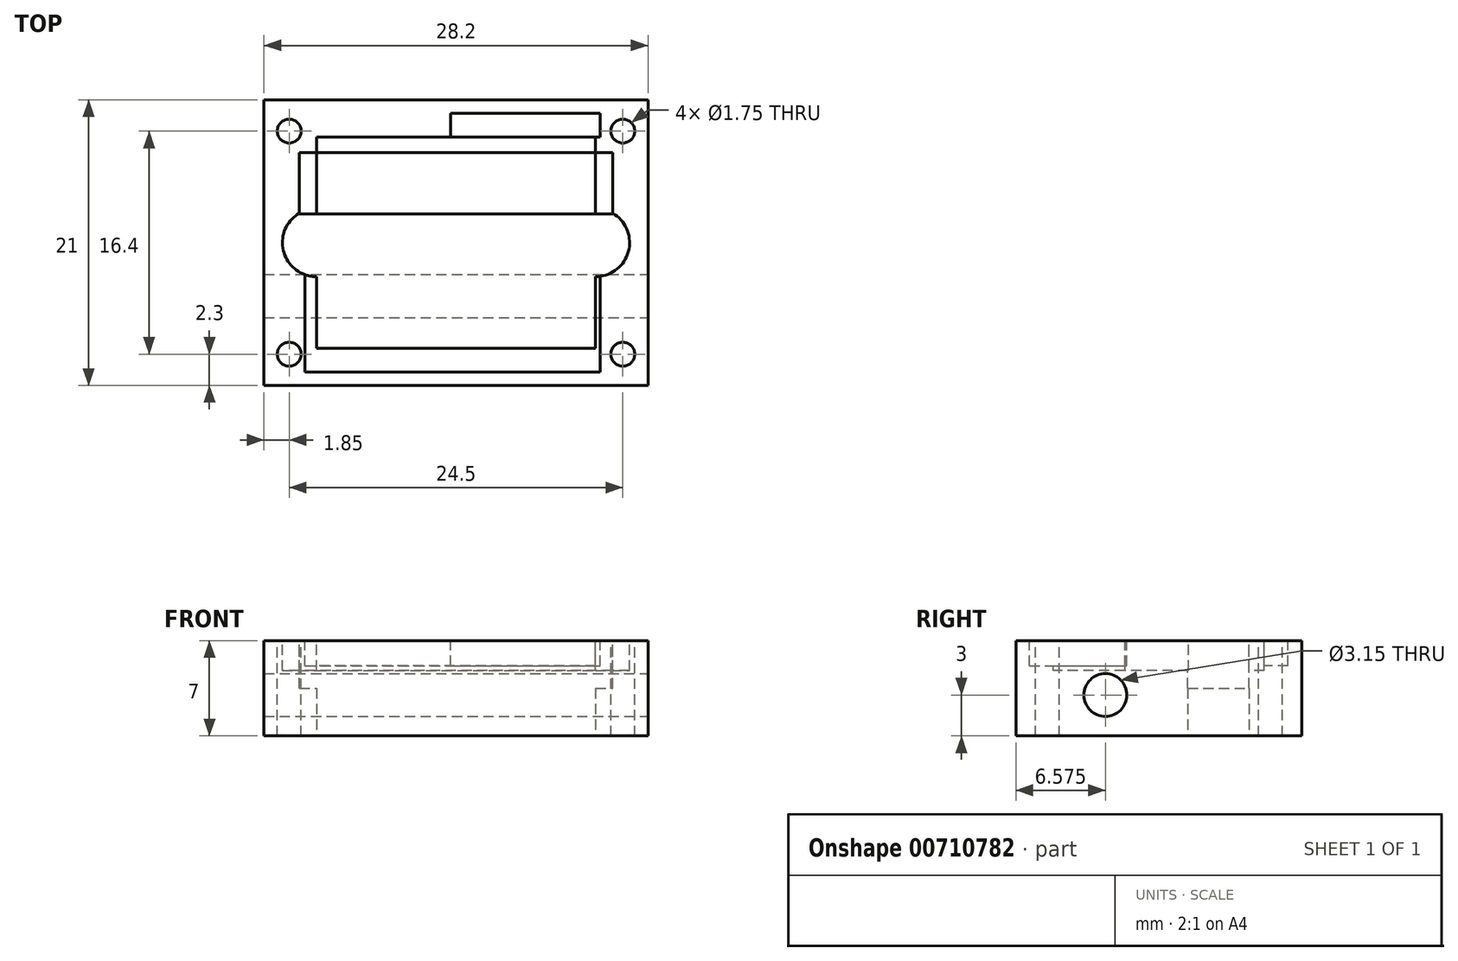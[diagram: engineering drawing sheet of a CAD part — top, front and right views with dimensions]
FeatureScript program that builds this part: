
annotation { "Feature Type Name" : "Feature", "Feature Type Description" : "" }
export const myFeature = defineFeature(function(context is Context, id is Id, definition is map)
    precondition{}
    {
        {
            var Q0;
            Q0=qCreatedBy(makeId("Top.planeOp"),FACE);
            var sketch = newSketch(context, id + "F0", { "sketchPlane" : qUnion([Q0])});
            skLineSegment(sketch, "E0.bottom", {"start": v(-14.1, 10.5) * mm, "end": v(14.1, 10.5) * mm});
            skLineSegment(sketch, "E0.top", {"start": v(-14.1, -10.5) * mm, "end": v(14.1, -10.5) * mm});
            skLineSegment(sketch, "E0.left", {"start": v(-14.1, 10.5) * mm, "end": v(-14.1, -10.5) * mm});
            skLineSegment(sketch, "E0.right", {"start": v(14.1, 10.5) * mm, "end": v(14.1, -10.5) * mm});
            skPoint(sketch, "E0.middle", {"position": v(0, 0) * mm});
            skSolve(sketch);
        }
        {
            var Q0;
            Q0 = qSketchRegion(id + "F0", true);
            extrude(context, id + "F1", {"entities" : qUnion([Q0]), "endBound" : BoundingType.SYMMETRIC, "depth" : 8 * mm, "offsetDistance" : 25 * mm});
        }
        {
            var Q0;
            Q0=makeQuery(id+"F1.opExtrude","CAP_FACE",FACE,{"disambiguationData":[OSD([sQuery(id+"F0.wireOp",EDGE,"E0.bottom"),sQuery(id+"F0.wireOp",EDGE,"E0.top"),sQuery(id+"F0.wireOp",EDGE,"E0.left"),sQuery(id+"F0.wireOp",EDGE,"E0.right")])],"isStart":false});
            var sketch = newSketch(context, id + "F2", { "sketchPlane" : qUnion([Q0])});
            skLineSegment(sketch, "E1.bottom", {"start": v(-10.25, 7.75) * mm, "end": v(10.25, 7.75) * mm});
            skLineSegment(sketch, "E1.top", {"start": v(-10.25, -7.75) * mm, "end": v(10.25, -7.75) * mm});
            skLineSegment(sketch, "E1.left", {"start": v(-10.25, 7.75) * mm, "end": v(-10.25, -7.75) * mm});
            skLineSegment(sketch, "E1.right", {"start": v(10.25, 7.75) * mm, "end": v(10.25, -7.75) * mm});
            skPoint(sketch, "E1.middle", {"position": v(0, 0) * mm});
            skCircle(sketch, "E2", {"center": v(-10.25, 0) * mm, "radius": 2.5 * mm});
            skCircle(sketch, "E3", {"center": v(10.25, 0) * mm, "radius": 2.5 * mm});
            skSolve(sketch);
        }
        {
            var Q0;
            Q0 = qSketchRegion(id + "F2", true);
            var Q1;
            Q1 = qSketchRegion(id + "F5", true);
            extrude(context, id + "F3", {"entities" : qUnion([Q0, Q1]), "operationType" : NewBodyOperationType.REMOVE, "oppositeDirection" : true, "depth" : 2.2 * mm, "offsetDistance" : 25 * mm});
        }
        {
            var Q0;
            Q0=makeQuery(id+"F1.opExtrude","CAP_FACE",FACE,{"disambiguationData":[OSD([sQuery(id+"F0.wireOp",EDGE,"E0.bottom"),sQuery(id+"F0.wireOp",EDGE,"E0.top"),sQuery(id+"F0.wireOp",EDGE,"E0.left"),sQuery(id+"F0.wireOp",EDGE,"E0.right")])],"isStart":false});
            var sketch = newSketch(context, id + "F4", { "sketchPlane" : qUnion([Q0])});
            skLineSegment(sketch, "E4.bottom", {"start": v(-12.25, 8.2) * mm, "end": v(12.25, 8.2) * mm});
            skLineSegment(sketch, "E4.top", {"start": v(-12.25, -8.2) * mm, "end": v(12.25, -8.2) * mm});
            skLineSegment(sketch, "E4.left", {"start": v(-12.25, 8.2) * mm, "end": v(-12.25, -8.2) * mm});
            skLineSegment(sketch, "E4.right", {"start": v(12.25, 8.2) * mm, "end": v(12.25, -8.2) * mm});
            skPoint(sketch, "E4.middle", {"position": v(0, 0) * mm});
            skSolve(sketch);
        }
        {
            var Q0;
            Q0=makeQuery(id+"F4.imprint","IMPRINT",FACE,{"disambiguationData":[TD([[makeQuery(id+"F4.imprint","IMPRINT",EDGE,{"derivedFrom":sQuery(id+"F4.wireOp",EDGE,"E4.bottom")}),1.0]])]});
            var sketch = newSketch(context, id + "F5", { "sketchPlane" : qUnion([Q0])});
            skCircle(sketch, "E5", {"center": v(-12.25, 8.2) * mm, "radius": 0.88 * mm});
            skCircle(sketch, "E6", {"center": v(12.25, 8.2) * mm, "radius": 0.88 * mm});
            skCircle(sketch, "E7", {"center": v(12.25, -8.2) * mm, "radius": 0.88 * mm});
            skCircle(sketch, "E8", {"center": v(-12.25, -8.2) * mm, "radius": 0.88 * mm});
            skSolve(sketch);
        }
        {
            var Q0;
            Q0 = qSketchRegion(id + "F5", true);
            extrude(context, id + "F6", {"entities" : qUnion([Q0]), "operationType" : NewBodyOperationType.REMOVE, "oppositeDirection" : true, "depth" : 25 * mm, "offsetDistance" : 25 * mm});
        }
        {
            var Q0;
            Q0=qCreatedBy(makeId("Top.planeOp"),FACE);
            var sketch = newSketch(context, id + "F7", { "sketchPlane" : qUnion([Q0])});
            skLineSegment(sketch, "E9.bottom", {"start": v(-10.25, 6.62) * mm, "end": v(10.25, 6.62) * mm});
            skLineSegment(sketch, "E9.top", {"start": v(-10.25, 2.12) * mm, "end": v(10.25, 2.12) * mm});
            skLineSegment(sketch, "E9.left", {"start": v(-10.25, 6.62) * mm, "end": v(-10.25, 2.12) * mm});
            skLineSegment(sketch, "E9.right", {"start": v(10.25, 6.62) * mm, "end": v(10.25, 2.12) * mm});
            skSolve(sketch);
        }
        {
            var Q0;
            Q0 = qSketchRegion(id + "F7", true);
            extrude(context, id + "F8", {"entities" : qUnion([Q0]), "operationType" : NewBodyOperationType.REMOVE, "endBound" : BoundingType.SYMMETRIC, "depth" : 55 * mm, "offsetDistance" : 25 * mm});
        }
        {
            var Q0;
            Q0=makeQuery(id+"F1.opExtrude","SWEPT_FACE",FACE,{"disambiguationData":[OSD([sQuery(id+"F0.wireOp",EDGE,"E0.right")])]});
            var sketch = newSketch(context, id + "F9", { "sketchPlane" : qUnion([Q0])});
            skCircle(sketch, "E10", {"center": v(-3.93, 0) * mm, "radius": 1.58 * mm});
            skSolve(sketch);
        }
        {
            var Q0;
            Q0 = qSketchRegion(id + "F9", true);
            extrude(context, id + "F10", {"entities" : qUnion([Q0]), "operationType" : NewBodyOperationType.REMOVE, "oppositeDirection" : true, "depth" : 29 * mm, "offsetDistance" : 25 * mm});
        }
        {
            var Q0;
            Q0=makeQuery(id+"F1.opExtrude","SWEPT_FACE",FACE,{"disambiguationData":[OSD([sQuery(id+"F0.wireOp",EDGE,"E0.right")])]});
            var sketch = newSketch(context, id + "F11", { "sketchPlane" : qUnion([Q0])});
            skLineSegment(sketch, "E11.bottom", {"start": v(-10.5, -4) * mm, "end": v(10.5, -4) * mm});
            skLineSegment(sketch, "E11.top", {"start": v(-10.5, -3) * mm, "end": v(10.5, -3) * mm});
            skLineSegment(sketch, "E11.left", {"start": v(-10.5, -4) * mm, "end": v(-10.5, -3) * mm});
            skLineSegment(sketch, "E11.right", {"start": v(10.5, -4) * mm, "end": v(10.5, -3) * mm});
            skSolve(sketch);
        }
        {
            var Q0;
            Q0 = qSketchRegion(id + "F11", true);
            extrude(context, id + "F12", {"entities" : qUnion([Q0]), "operationType" : NewBodyOperationType.REMOVE, "oppositeDirection" : true, "depth" : 28.2 * mm, "offsetDistance" : 25 * mm});
        }
        {
            var Q0;
            {var subQ4=sQuery(id+"F4.wireOp",EDGE,"E4.bottom");Q0=makeQuery(id+"F4.imprint","IMPRINT",FACE,{"disambiguationData":[TD([[makeQuery(id+"F4.imprint","IMPRINT",EDGE,{"derivedFrom":subQ4}),1.0]])]});}
            var sketch = newSketch(context, id + "F13", { "sketchPlane" : qUnion([Q0])});
            skLineSegment(sketch, "E12.bottom", {"start": v(-11.5, 6.62) * mm, "end": v(11.5, 6.62) * mm});
            skLineSegment(sketch, "E12.top", {"start": v(-11.5, 2.12) * mm, "end": v(11.5, 2.12) * mm});
            skLineSegment(sketch, "E12.left", {"start": v(-11.5, 6.62) * mm, "end": v(-11.5, 2.12) * mm});
            skLineSegment(sketch, "E12.right", {"start": v(11.5, 6.62) * mm, "end": v(11.5, 2.12) * mm});
            skSolve(sketch);
        }
        {
            var Q0;
            Q0 = qSketchRegion(id + "F13", true);
            extrude(context, id + "F14", {"entities" : qUnion([Q0]), "operationType" : NewBodyOperationType.REMOVE, "oppositeDirection" : true, "depth" : 3.5 * mm, "offsetDistance" : 25 * mm});
        }
        {
            var Q0;
            Q0 = qSketchRegion(id + "F13", true);
            extrude(context, id + "F15", {"entities" : qUnion([Q0]), "operationType" : NewBodyOperationType.REMOVE, "oppositeDirection" : true, "depth" : 3 * mm, "offsetDistance" : 25 * mm});
        }
        {
            var Q0;
            {var subQ4=sQuery(id+"F4.wireOp",EDGE,"E4.bottom");Q0=makeQuery(id+"F4.imprint","IMPRINT",FACE,{"disambiguationData":[TD([[makeQuery(id+"F4.imprint","IMPRINT",EDGE,{"derivedFrom":subQ4}),1.0]])]});}
            var sketch = newSketch(context, id + "F16", { "sketchPlane" : qUnion([Q0])});
            skLineSegment(sketch, "E13.bottom", {"start": v(-0.4, 9.5) * mm, "end": v(10.6, 9.5) * mm});
            skLineSegment(sketch, "E13.top", {"start": v(-0.4, 7.75) * mm, "end": v(10.6, 7.75) * mm});
            skLineSegment(sketch, "E13.left", {"start": v(-0.4, 9.5) * mm, "end": v(-0.4, 7.75) * mm});
            skLineSegment(sketch, "E13.right", {"start": v(10.6, 9.5) * mm, "end": v(10.6, 7.75) * mm});
            skSolve(sketch);
        }
        {
            var Q0;
            Q0 = qSketchRegion(id + "F16", true);
            extrude(context, id + "F17", {"entities" : qUnion([Q0]), "operationType" : NewBodyOperationType.REMOVE, "oppositeDirection" : true, "depth" : 1.85 * mm, "offsetDistance" : 25 * mm});
        }
        {
            var Q0;
            {var subQ4=sQuery(id+"F4.wireOp",EDGE,"E4.bottom");Q0=makeQuery(id+"F4.imprint","IMPRINT",FACE,{"disambiguationData":[TD([[makeQuery(id+"F4.imprint","IMPRINT",EDGE,{"derivedFrom":subQ4}),1.0]])]});}
            var sketch = newSketch(context, id + "F18", { "sketchPlane" : qUnion([Q0])});
            skLineSegment(sketch, "E14.bottom", {"start": v(-11.1, -9.5) * mm, "end": v(10.6, -9.5) * mm});
            skLineSegment(sketch, "E14.top", {"start": v(-11.1, -1.5) * mm, "end": v(10.6, -1.5) * mm});
            skLineSegment(sketch, "E14.left", {"start": v(-11.1, -9.5) * mm, "end": v(-11.1, -1.5) * mm});
            skLineSegment(sketch, "E14.right", {"start": v(10.6, -9.5) * mm, "end": v(10.6, -1.5) * mm});
            skSolve(sketch);
        }
        {
            var Q0;
            Q0 = qSketchRegion(id + "F18", true);
            extrude(context, id + "F19", {"entities" : qUnion([Q0]), "operationType" : NewBodyOperationType.REMOVE, "oppositeDirection" : true, "depth" : 1.85 * mm, "offsetDistance" : 25 * mm});
        }
    });
